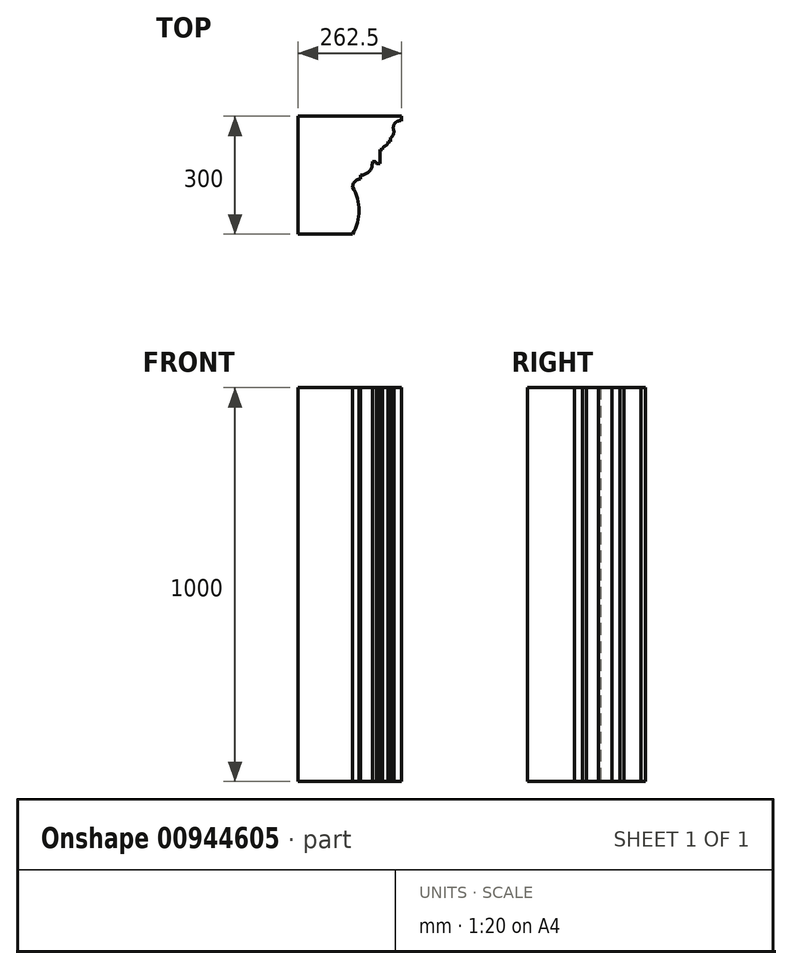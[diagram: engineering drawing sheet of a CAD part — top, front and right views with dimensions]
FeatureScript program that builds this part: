
annotation { "Feature Type Name" : "Feature", "Feature Type Description" : "" }
export const myFeature = defineFeature(function(context is Context, id is Id, definition is map)
    precondition{}
    {
        {
            var Q0;
            Q0=qCreatedBy(makeId("Top.planeOp"),FACE);
            var sketch = newSketch(context, id + "F0", { "sketchPlane" : qUnion([Q0])});
            skLineSegment(sketch, "E0", {"start": v(-136.78, 120) * mm, "end": v(125.72, 120) * mm});
            skLineSegment(sketch, "E1", {"start": v(125.72, 120) * mm, "end": v(125.72, 108) * mm});
            skLineSegment(sketch, "E2", {"start": v(-136.78, 120) * mm, "end": v(-136.78, -180) * mm});
            skLineSegment(sketch, "E3", {"start": v(-136.78, -180) * mm, "end": v(1.72, -180) * mm});
            skLineSegment(sketch, "E4", {"start": v(1.72, -180) * mm, "end": v(1.72, -60) * mm, "construction": true});
            skLineSegment(sketch, "E5", {"start": v(1.72, -120) * mm, "end": v(-98.28, -120) * mm, "construction": true});
            skArc(sketch, "E6", {"start": v(1.72, -180) * mm, "mid": v(18.34, -120) * mm, "end": v(1.72, -60) * mm});
            skLineSegment(sketch, "E7", {"start": v(21.72, -40) * mm, "end": v(21.72, -30) * mm});
            skArc(sketch, "E8", {"start": v(1.72, -60) * mm, "mid": v(7.57, -45.86) * mm, "end": v(21.72, -40) * mm});
            skLineSegment(sketch, "E9", {"start": v(21.72, -30) * mm, "end": v(21.72, 0) * mm, "construction": true});
            skArc(sketch, "E10", {"start": v(21.72, -30) * mm, "mid": v(42.93, -21.21) * mm, "end": v(51.72, 0) * mm});
            skLineSegment(sketch, "E11", {"start": v(51.72, 0) * mm, "end": v(51.72, 5) * mm});
            skLineSegment(sketch, "E12", {"start": v(51.72, 5) * mm, "end": v(56.72, 5) * mm});
            skLineSegment(sketch, "E13", {"start": v(56.72, 5) * mm, "end": v(61.72, 5) * mm, "construction": true});
            skLineSegment(sketch, "E14", {"start": v(61.72, 5) * mm, "end": v(61.72, 0) * mm, "construction": true});
            skArc(sketch, "E15", {"start": v(56.72, 5) * mm, "mid": v(60.25, 3.54) * mm, "end": v(61.72, 0) * mm});
            skLineSegment(sketch, "E16", {"start": v(61.72, 0) * mm, "end": v(71.72, 0) * mm});
            skLineSegment(sketch, "E17", {"start": v(71.72, 0) * mm, "end": v(71.72, 35) * mm});
            skLineSegment(sketch, "E18", {"start": v(71.72, 35) * mm, "end": v(77.72, 35) * mm});
            skLineSegment(sketch, "E19", {"start": v(77.72, 35) * mm, "end": v(77.72, 45) * mm, "construction": true});
            skLineSegment(sketch, "E20", {"start": v(77.72, 45) * mm, "end": v(77.72, 55) * mm, "construction": true});
            skArc(sketch, "E21", {"start": v(84.74, 44.55) * mm, "mid": v(79.66, 40.92) * mm, "end": v(77.72, 35) * mm});
            skArc(sketch, "E22", {"start": v(84.74, 44.55) * mm, "mid": v(90.07, 48.54) * mm, "end": v(91.72, 55) * mm});
            skLineSegment(sketch, "E23", {"start": v(91.72, 55) * mm, "end": v(97.72, 55) * mm});
            skLineSegment(sketch, "E24", {"start": v(97.72, 55) * mm, "end": v(97.72, 65) * mm});
            skArc(sketch, "E25", {"start": v(97.72, 65) * mm, "mid": v(105.35, 73.84) * mm, "end": v(105.72, 85.5) * mm});
            skArc(sketch, "E26", {"start": v(125.72, 108) * mm, "mid": v(109.32, 102.45) * mm, "end": v(105.72, 85.5) * mm});
            skSolve(sketch);
        }
        {
            var Q0;
            Q0=makeQuery(id+"F0.imprint","IMPRINT",FACE,{"disambiguationData":[TD([[makeQuery(id+"F0.imprint","IMPRINT",EDGE,{"derivedFrom":sQuery(id+"F0.wireOp",EDGE,"E0")}),-1.0]])]});
            extrude(context, id + "F1", {"entities" : qUnion([Q0]), "depth" : 1000 * mm, "offsetDistance" : 25 * mm});
        }
    });
